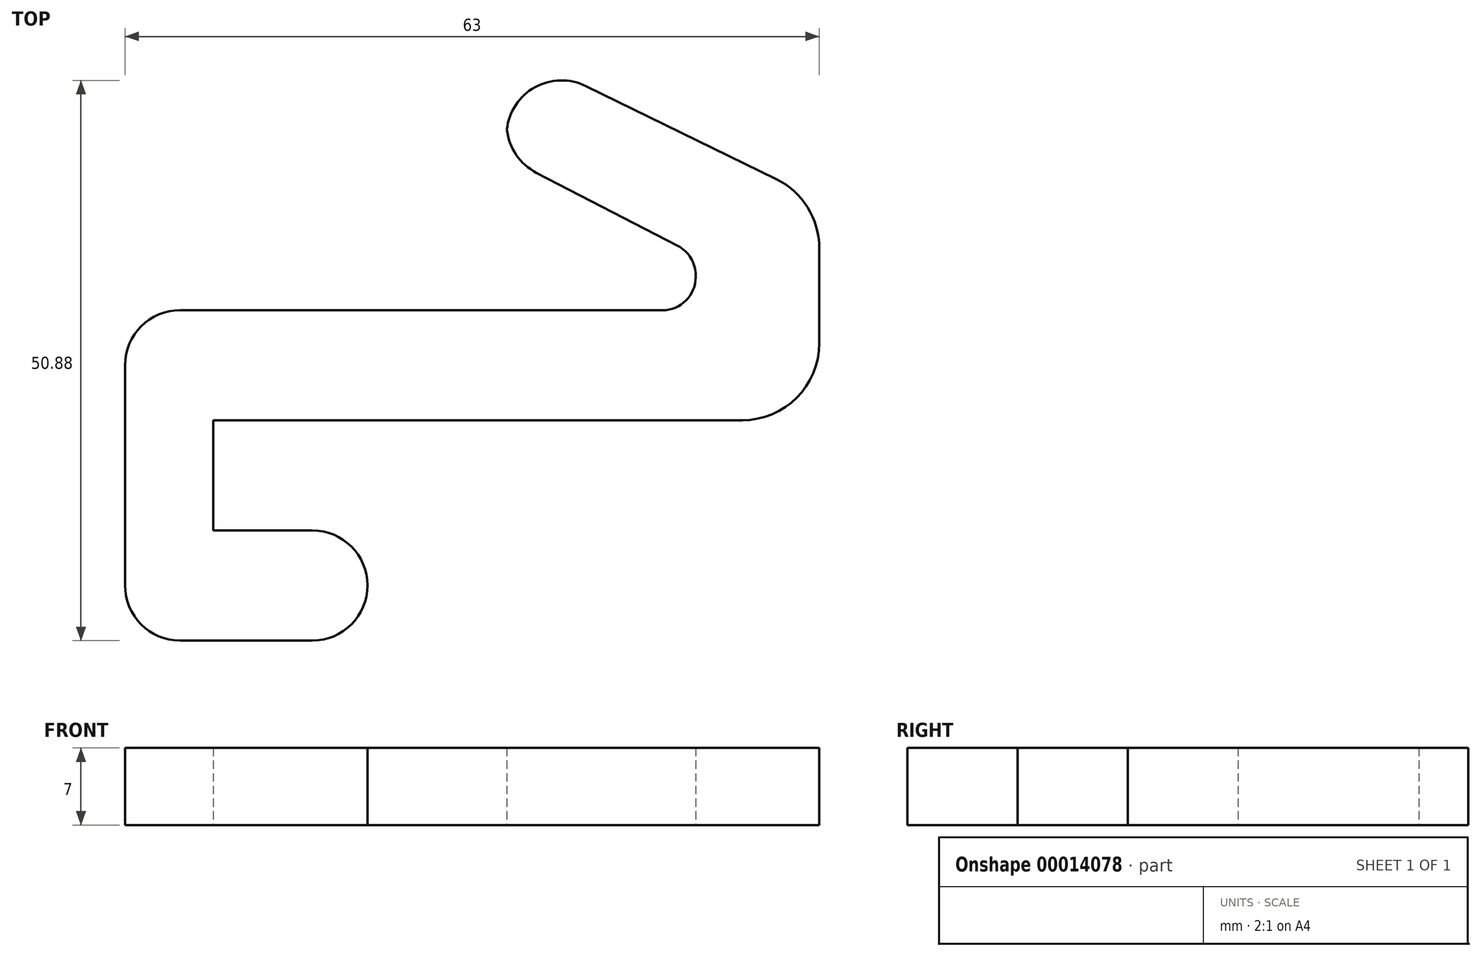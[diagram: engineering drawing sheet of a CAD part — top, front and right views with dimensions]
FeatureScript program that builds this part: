
annotation { "Feature Type Name" : "Feature", "Feature Type Description" : "" }
export const myFeature = defineFeature(function(context is Context, id is Id, definition is map)
    precondition{}
    {
        {
            var Q0;
            Q0=qCreatedBy(makeId("Top.planeOp"),FACE);
            var sketch = newSketch(context, id + "F0", { "sketchPlane" : qUnion([Q0])});
            skLineSegment(sketch, "E0", {"start": v(-21.24, -23.19) * mm, "end": v(-7.24, -23.19) * mm});
            skLineSegment(sketch, "E1", {"start": v(-7.24, -23.19) * mm, "end": v(-7.24, -13.19) * mm});
            skLineSegment(sketch, "E2", {"start": v(-7.24, -13.19) * mm, "end": v(-21.24, -13.19) * mm});
            skLineSegment(sketch, "E3", {"start": v(-21.24, -13.19) * mm, "end": v(-21.24, -3.19) * mm});
            skLineSegment(sketch, "E4", {"start": v(-21.24, -3.19) * mm, "end": v(33.76, -3.19) * mm});
            skLineSegment(sketch, "E5", {"start": v(33.76, -3.19) * mm, "end": v(33.76, 16.81) * mm});
            skLineSegment(sketch, "E6", {"start": v(33.76, 16.81) * mm, "end": v(5.38, 30.7) * mm});
            skLineSegment(sketch, "E7", {"start": v(5.38, 30.7) * mm, "end": v(5.38, 20.7) * mm});
            skLineSegment(sketch, "E8", {"start": v(5.38, 20.7) * mm, "end": v(22.54, 11.81) * mm});
            skLineSegment(sketch, "E9", {"start": v(22.54, 11.81) * mm, "end": v(22.54, 6.81) * mm});
            skLineSegment(sketch, "E10", {"start": v(22.54, 6.81) * mm, "end": v(-21.24, 6.81) * mm});
            skLineSegment(sketch, "E11", {"start": v(-21.24, 6.81) * mm, "end": v(-29.24, 6.81) * mm});
            skLineSegment(sketch, "E12", {"start": v(-29.24, 6.81) * mm, "end": v(-29.24, -23.19) * mm});
            skLineSegment(sketch, "E13", {"start": v(-29.24, -23.19) * mm, "end": v(-21.24, -23.19) * mm});
            skLineSegment(sketch, "E14", {"start": v(22.54, 6.81) * mm, "end": v(22.54, -3.19) * mm});
            skLineSegment(sketch, "E15", {"start": v(-21.24, -13.19) * mm, "end": v(-29.24, -13.19) * mm});
            skSolve(sketch);
        }
        {
            var Q0;
            Q0=makeQuery(id+"F0.imprint","IMPRINT",FACE,{"disambiguationData":[TD([[makeQuery(id+"F0.imprint","IMPRINT",EDGE,{"derivedFrom":sQuery(id+"F0.wireOp",EDGE,"E0")}),1.0]])]});
            var Q1;
            {var subQ5=sQuery(id+"F0.wireOp",EDGE,"E3");Q1=makeQuery(id+"F0.imprint","IMPRINT",FACE,{"disambiguationData":[TD([[makeQuery(id+"F0.imprint","IMPRINT",EDGE,{"derivedFrom":subQ5}),1.0]])]});}
            var Q2;
            {var subQ1=sQuery(id+"F0.wireOp",EDGE,"E5");Q2=makeQuery(id+"F0.imprint","IMPRINT",FACE,{"disambiguationData":[TD([[makeQuery(id+"F0.imprint","IMPRINT",EDGE,{"derivedFrom":subQ1}),1.0]])]});}
            extrude(context, id + "F1", {"entities" : qUnion([Q0, Q1, Q2]), "depth" : 7 * mm});
        }
        {
            var Q0;
            Q0=makeQuery(id+"F1.opExtrude","SWEPT_EDGE",EDGE,{"disambiguationData":[OSD([sQuery(id+"F0.wireOp",EDGE,"E4"),sQuery(id+"F0.wireOp",EDGE,"E5")])]});
            var Q1;
            Q1=makeQuery(id+"F1.opExtrude","SWEPT_EDGE",EDGE,{"disambiguationData":[OSD([sQuery(id+"F0.wireOp",EDGE,"E5"),sQuery(id+"F0.wireOp",EDGE,"E6")])]});
            fillet(context, id + "F2", {"entities" : qUnion([Q0, Q1]), "radius" : 7 * mm, "tangentPropagation" : true, "allowEdgeOverflow" : false});
        }
        {
            var Q0;
            Q0=makeQuery(id+"F1.opExtrude","SWEPT_EDGE",EDGE,{"disambiguationData":[OSD([sQuery(id+"F0.wireOp",EDGE,"E6"),sQuery(id+"F0.wireOp",EDGE,"E7")])]});
            var Q1;
            Q1=makeQuery(id+"F1.opExtrude","SWEPT_EDGE",EDGE,{"disambiguationData":[OSD([sQuery(id+"F0.wireOp",EDGE,"E7"),sQuery(id+"F0.wireOp",EDGE,"E8")])]});
            var Q2;
            Q2=makeQuery(id+"F1.opExtrude","SWEPT_EDGE",EDGE,{"disambiguationData":[OSD([sQuery(id+"F0.wireOp",EDGE,"E11"),sQuery(id+"F0.wireOp",EDGE,"E12")])]});
            var Q3;
            Q3=makeQuery(id+"F1.opExtrude","SWEPT_EDGE",EDGE,{"disambiguationData":[OSD([sQuery(id+"F0.wireOp",EDGE,"E12"),sQuery(id+"F0.wireOp",EDGE,"E13")])]});
            fillet(context, id + "F3", {"entities" : qUnion([Q0, Q1, Q2, Q3]), "radius" : 5 * mm, "tangentPropagation" : true, "allowEdgeOverflow" : false});
        }
        {
            var Q0;
            Q0=makeQuery(id+"F1.opExtrude","SWEPT_EDGE",EDGE,{"disambiguationData":[OSD([sQuery(id+"F0.wireOp",EDGE,"E9"),sQuery(id+"F0.wireOp",EDGE,"E10"),sQuery(id+"F0.wireOp",EDGE,"E14")])]});
            var Q1;
            Q1=makeQuery(id+"F1.opExtrude","SWEPT_EDGE",EDGE,{"disambiguationData":[OSD([sQuery(id+"F0.wireOp",EDGE,"E8"),sQuery(id+"F0.wireOp",EDGE,"E9")])]});
            fillet(context, id + "F4", {"entities" : qUnion([Q0, Q1]), "radius" : 3 * mm, "tangentPropagation" : true, "allowEdgeOverflow" : false});
        }
        {
            var Q0;
            Q0=makeQuery(id+"F1.opExtrude","SWEPT_EDGE",EDGE,{"disambiguationData":[OSD([sQuery(id+"F0.wireOp",EDGE,"E0"),sQuery(id+"F0.wireOp",EDGE,"E1")])]});
            var Q1;
            Q1=makeQuery(id+"F1.opExtrude","SWEPT_EDGE",EDGE,{"disambiguationData":[OSD([sQuery(id+"F0.wireOp",EDGE,"E1"),sQuery(id+"F0.wireOp",EDGE,"E2")])]});
            fillet(context, id + "F5", {"entities" : qUnion([Q0, Q1]), "radius" : 5 * mm, "tangentPropagation" : true, "allowEdgeOverflow" : false});
        }
    });
